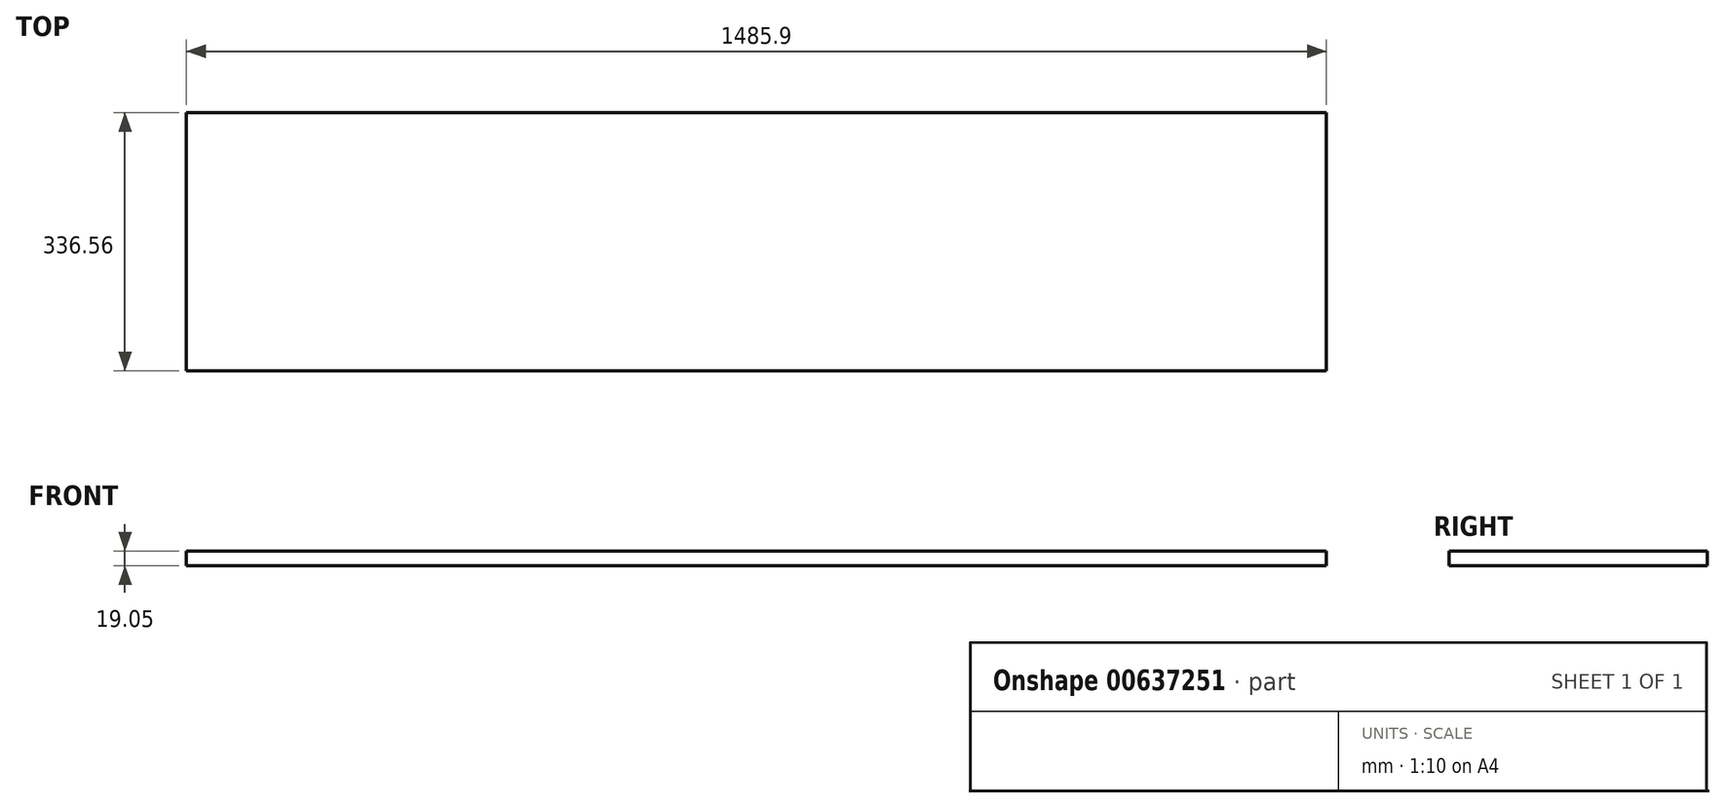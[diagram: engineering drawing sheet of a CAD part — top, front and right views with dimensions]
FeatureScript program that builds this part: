
annotation { "Feature Type Name" : "Feature", "Feature Type Description" : "" }
export const myFeature = defineFeature(function(context is Context, id is Id, definition is map)
    precondition{}
    {
        {
            var Q0;
            Q0=qCreatedBy(makeId("Top.planeOp"),FACE);
            var sketch = newSketch(context, id + "F0", { "sketchPlane" : qUnion([Q0])});
            skLineSegment(sketch, "E0.bottom", {"start": v(742.95, 168.28) * mm, "end": v(-742.95, 168.28) * mm});
            skLineSegment(sketch, "E0.top", {"start": v(742.95, -168.27) * mm, "end": v(-742.95, -168.27) * mm});
            skLineSegment(sketch, "E0.left", {"start": v(742.95, 168.28) * mm, "end": v(742.95, -168.27) * mm});
            skLineSegment(sketch, "E0.right", {"start": v(-742.95, 168.28) * mm, "end": v(-742.95, -168.27) * mm});
            skPoint(sketch, "E0.middle", {"position": v(0, 0) * mm});
            skSolve(sketch);
        }
        {
            var Q0;
            Q0=makeQuery(id+"F0.imprint","IMPRINT",FACE,{"disambiguationData":[TD([[makeQuery(id+"F0.imprint","IMPRINT",EDGE,{"derivedFrom":sQuery(id+"F0.wireOp",EDGE,"E0.bottom")}),1.0]])]});
            extrude(context, id + "F1", {"entities" : qUnion([Q0]), "depth" : 19.05 * mm, "offsetDistance" : 25.4 * mm});
        }
    });
